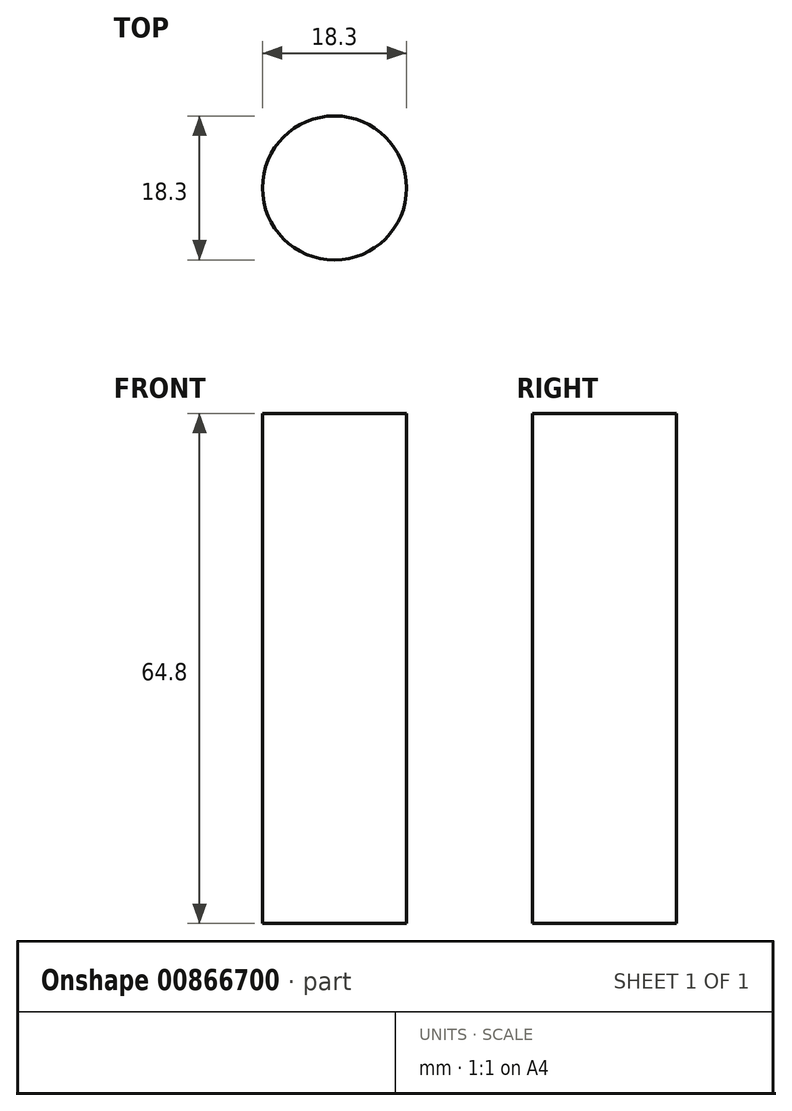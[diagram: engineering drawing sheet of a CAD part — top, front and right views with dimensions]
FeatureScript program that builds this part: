
annotation { "Feature Type Name" : "Feature", "Feature Type Description" : "" }
export const myFeature = defineFeature(function(context is Context, id is Id, definition is map)
    precondition{}
    {
        {
            var Q0;
            Q0=qCreatedBy(makeId("Top.planeOp"),FACE);
            var sketch = newSketch(context, id + "F0", { "sketchPlane" : qUnion([Q0])});
            skCircle(sketch, "E0", {"center": v(0, 0) * mm, "radius": 9.15 * mm});
            skSolve(sketch);
        }
        {
            var Q0;
            Q0=makeQuery(id+"F0.imprint","IMPRINT",FACE,{"disambiguationData":[TD([[makeQuery(id+"F0.imprint","IMPRINT",EDGE,{"derivedFrom":sQuery(id+"F0.wireOp",EDGE,"E0")}),1.0]])]});
            extrude(context, id + "F1", {"entities" : qUnion([Q0]), "depth" : 64.8 * mm, "offsetDistance" : 25 * mm});
        }
    });
